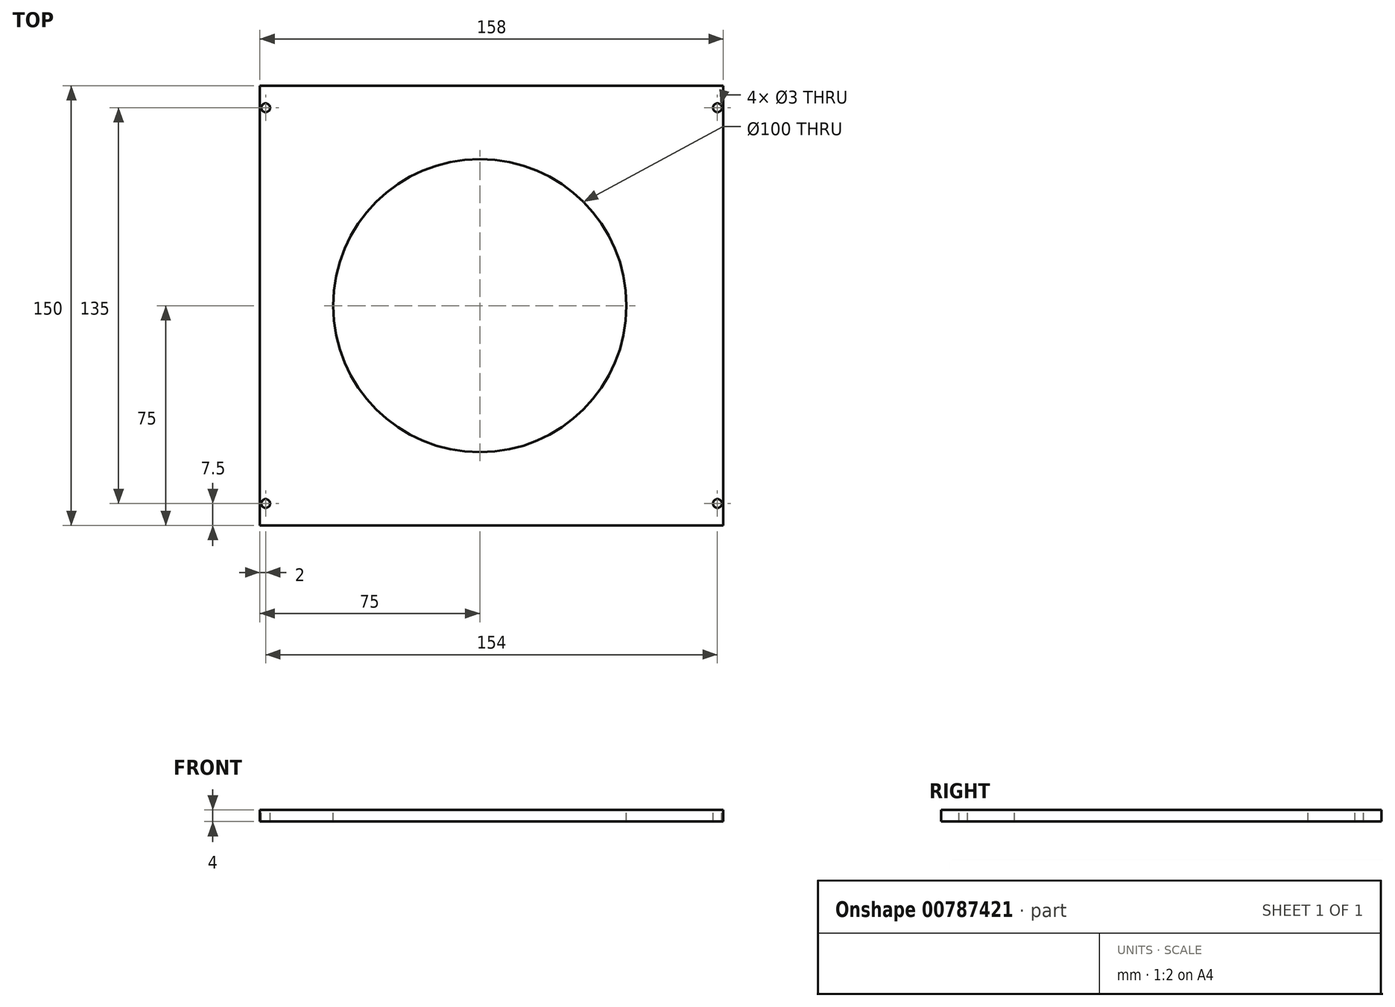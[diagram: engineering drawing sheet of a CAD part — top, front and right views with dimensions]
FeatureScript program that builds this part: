
annotation { "Feature Type Name" : "Feature", "Feature Type Description" : "" }
export const myFeature = defineFeature(function(context is Context, id is Id, definition is map)
    precondition{}
    {
        {
            var Q0;
            Q0=qCreatedBy(makeId("Top.planeOp"),FACE);
            var sketch = newSketch(context, id + "F0", { "sketchPlane" : qUnion([Q0])});
            skLineSegment(sketch, "E0.bottom", {"start": v(0, 0) * mm, "end": v(-158, 0) * mm});
            skLineSegment(sketch, "E0.top", {"start": v(0, -150) * mm, "end": v(-158, -150) * mm});
            skLineSegment(sketch, "E0.left", {"start": v(0, 0) * mm, "end": v(0, -150) * mm});
            skLineSegment(sketch, "E0.right", {"start": v(-158, 0) * mm, "end": v(-158, -150) * mm});
            skSolve(sketch);
        }
        {
            var Q0;
            Q0=makeQuery(id+"F0.imprint","IMPRINT",FACE,{"disambiguationData":[TD([[makeQuery(id+"F0.imprint","IMPRINT",EDGE,{"derivedFrom":sQuery(id+"F0.wireOp",EDGE,"E0.bottom")}),1.0]])]});
            extrude(context, id + "F1", {"entities" : qUnion([Q0]), "depth" : 4 * mm, "offsetDistance" : 25 * mm});
        }
        {
            var Q0;
            Q0=makeQuery(id+"F1.opExtrude","CAP_FACE",FACE,{"disambiguationData":[OSD([sQuery(id+"F0.wireOp",EDGE,"E0.bottom"),sQuery(id+"F0.wireOp",EDGE,"E0.top"),sQuery(id+"F0.wireOp",EDGE,"E0.left"),sQuery(id+"F0.wireOp",EDGE,"E0.right")])],"isStart":false});
            var sketch = newSketch(context, id + "F2", { "sketchPlane" : qUnion([Q0])});
            skCircle(sketch, "E1", {"center": v(-156, -142.5) * mm, "radius": 1.5 * mm});
            skLineSegment(sketch, "E2", {"start": v(-158, -75) * mm, "end": v(0, -75) * mm, "construction": true});
            skLineSegment(sketch, "E3", {"start": v(-79, 0) * mm, "end": v(-79, -150) * mm, "construction": true});
            skCircle(sketch, "E4.MirrorC", {"center": v(-2, -142.5) * mm, "radius": 1.5 * mm});
            skLineSegment(sketch, "E5.MirrorCS", {"start": v(0, -75) * mm, "end": v(-158, -75) * mm, "construction": true});
            skCircle(sketch, "E6.MirrorC", {"center": v(-156, -7.5) * mm, "radius": 1.5 * mm});
            skCircle(sketch, "E7.MirrorC", {"center": v(-2, -7.5) * mm, "radius": 1.5 * mm});
            skSolve(sketch);
        }
        {
            var Q0;
            Q0 = qSketchRegion(id + "F2", true);
            extrude(context, id + "F3", {"entities" : qUnion([Q0]), "operationType" : NewBodyOperationType.REMOVE, "oppositeDirection" : true, "depth" : 25 * mm, "offsetDistance" : 25 * mm});
        }
        {
            var Q0;
            Q0=makeQuery(id+"F1.opExtrude","CAP_FACE",FACE,{"disambiguationData":[OSD([sQuery(id+"F0.wireOp",EDGE,"E0.bottom"),sQuery(id+"F0.wireOp",EDGE,"E0.top"),sQuery(id+"F0.wireOp",EDGE,"E0.left"),sQuery(id+"F0.wireOp",EDGE,"E0.right")])],"isStart":false});
            var sketch = newSketch(context, id + "F4", { "sketchPlane" : qUnion([Q0])});
            skCircle(sketch, "E8", {"center": v(-83, -75) * mm, "radius": 50 * mm});
            skSolve(sketch);
        }
        {
            var Q0;
            Q0 = qSketchRegion(id + "F4", true);
            extrude(context, id + "F5", {"entities" : qUnion([Q0]), "operationType" : NewBodyOperationType.REMOVE, "oppositeDirection" : true, "depth" : 25 * mm, "offsetDistance" : 25 * mm});
        }
    });
